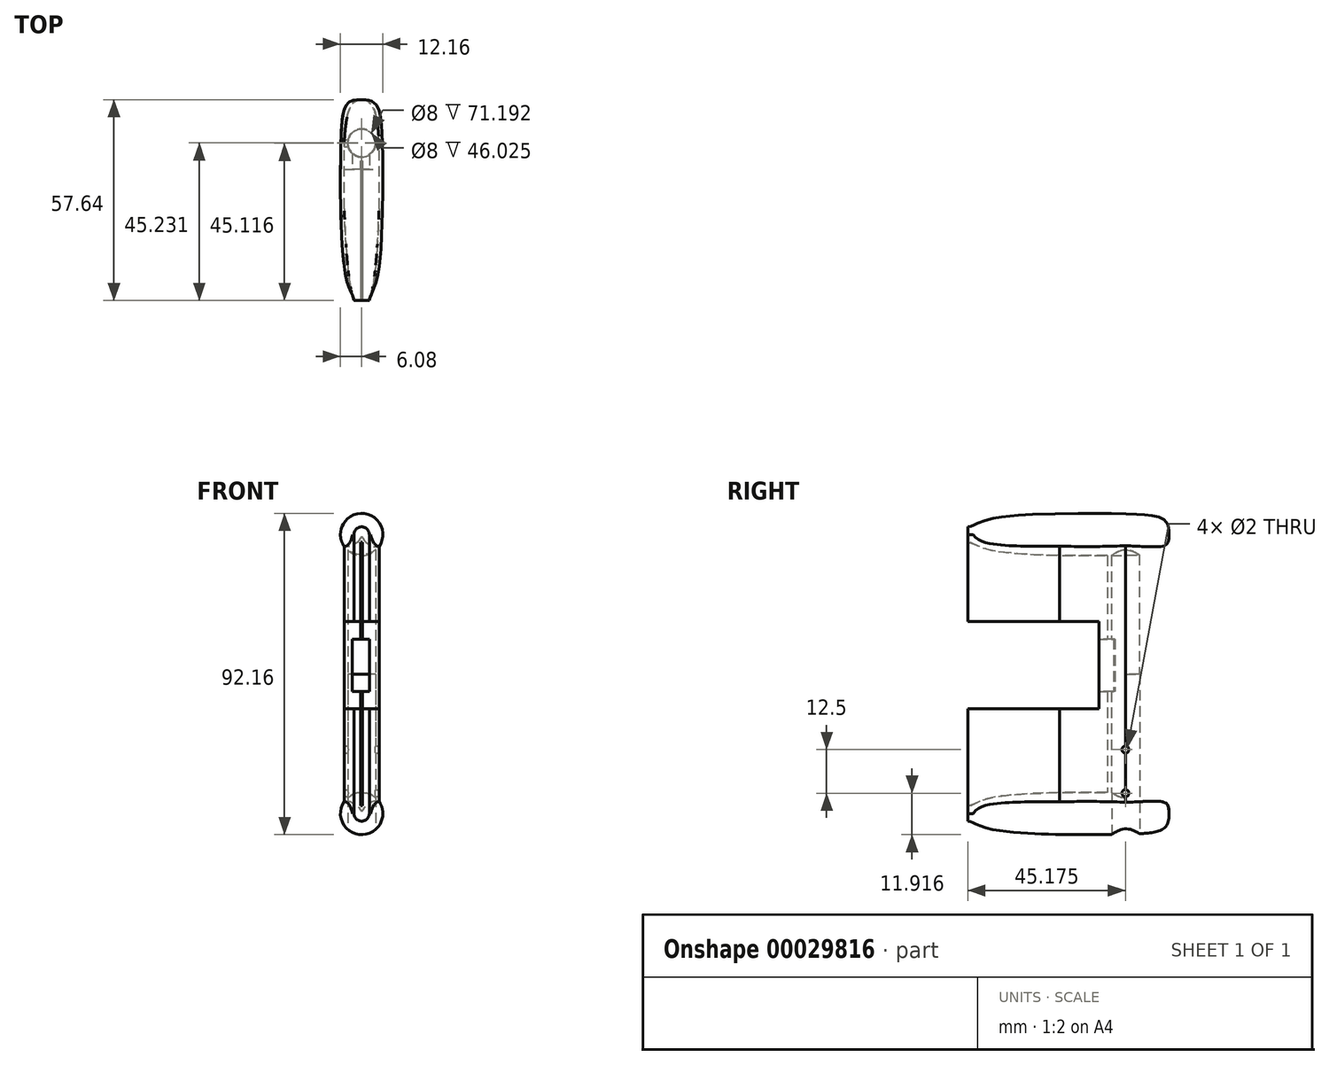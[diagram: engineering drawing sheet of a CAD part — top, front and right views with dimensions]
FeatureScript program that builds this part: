
annotation { "Feature Type Name" : "Feature", "Feature Type Description" : "" }
export const myFeature = defineFeature(function(context is Context, id is Id, definition is map)
    precondition{}
    {
        {
            var Q0;
            Q0=qCreatedBy(makeId("Top.planeOp"),FACE);
            var sketch = newSketch(context, id + "F0", { "sketchPlane" : qUnion([Q0])});
            skLineSegment(sketch, "E0", {"start": v(0, 90) * mm, "end": v(5, 90) * mm});
            skLineSegment(sketch, "E1", {"start": v(5, 90) * mm, "end": v(5, 10) * mm});
            skLineSegment(sketch, "E2", {"start": v(5, 10) * mm, "end": v(90, 10) * mm});
            skLineSegment(sketch, "E3", {"start": v(90, 10) * mm, "end": v(90, 0) * mm});
            skLineSegment(sketch, "E4", {"start": v(90, 0) * mm, "end": v(0, 0) * mm});
            skLineSegment(sketch, "E5.MirrorCS", {"start": v(0, 90) * mm, "end": v(-5, 90) * mm});
            skLineSegment(sketch, "E6.MirrorCS", {"start": v(-5, 90) * mm, "end": v(-5, 10) * mm});
            skLineSegment(sketch, "E7.MirrorCS", {"start": v(-5, 10) * mm, "end": v(-90, 10) * mm});
            skLineSegment(sketch, "E8.MirrorCS", {"start": v(-90, 10) * mm, "end": v(-90, 0) * mm});
            skLineSegment(sketch, "E9.MirrorCS", {"start": v(-90, 0) * mm, "end": v(0, 0) * mm});
            skSolve(sketch);
        }
        {
            var Q0;
            Q0=makeQuery(id+"F0.imprint","IMPRINT",FACE,{"disambiguationData":[TD([[makeQuery(id+"F0.imprint","IMPRINT",EDGE,{"derivedFrom":sQuery(id+"F0.wireOp",EDGE,"E0")}),-1.0]])]});
            extrude(context, id + "F1", {"entities" : qUnion([Q0]), "depth" : 10 * mm});
        }
        {
            var Q0;
            Q0=makeQuery(id+"F1.opExtrude","CAP_FACE",FACE,{"disambiguationData":[OSD([sQuery(id+"F0.wireOp",EDGE,"E0"),sQuery(id+"F0.wireOp",EDGE,"E1"),sQuery(id+"F0.wireOp",EDGE,"E2"),sQuery(id+"F0.wireOp",EDGE,"E3"),sQuery(id+"F0.wireOp",EDGE,"E4"),sQuery(id+"F0.wireOp",EDGE,"E5.MirrorCS"),sQuery(id+"F0.wireOp",EDGE,"E6.MirrorCS"),sQuery(id+"F0.wireOp",EDGE,"E7.MirrorCS"),sQuery(id+"F0.wireOp",EDGE,"E8.MirrorCS"),sQuery(id+"F0.wireOp",EDGE,"E9.MirrorCS")])],"isStart":false});
            var sketch = newSketch(context, id + "F2", { "sketchPlane" : qUnion([Q0])});
            skLineSegment(sketch, "E10.bottom", {"start": v(-5, 80) * mm, "end": v(5, 80) * mm});
            skLineSegment(sketch, "E10.top", {"start": v(-5, 70) * mm, "end": v(5, 70) * mm});
            skLineSegment(sketch, "E10.left", {"start": v(-5, 80) * mm, "end": v(-5, 70) * mm});
            skLineSegment(sketch, "E10.right", {"start": v(5, 80) * mm, "end": v(5, 70) * mm});
            skSolve(sketch);
        }
        {
            var Q0;
            Q0=makeQuery(id+"F2.imprint","IMPRINT",FACE,{"disambiguationData":[TD([[makeQuery(id+"F2.imprint","IMPRINT",EDGE,{"derivedFrom":sQuery(id+"F2.wireOp",EDGE,"E10.bottom")}),-1.0]])]});
            extrude(context, id + "F3", {"entities" : qUnion([Q0]), "operationType" : NewBodyOperationType.ADD, "depth" : 10 * mm});
        }
        {
            var Q0;
            {var subQ0=sQuery(id+"F0.wireOp",EDGE,"E1");var subQ1=sQuery(id+"F0.wireOp",EDGE,"E2");var subQ2=sQuery(id+"F0.wireOp",EDGE,"E3");var subQ3=sQuery(id+"F0.wireOp",EDGE,"E4");var subQ4=sQuery(id+"F0.wireOp",EDGE,"E6.MirrorCS");var subQ5=sQuery(id+"F0.wireOp",EDGE,"E7.MirrorCS");var subQ6=sQuery(id+"F0.wireOp",EDGE,"E8.MirrorCS");var subQ7=sQuery(id+"F0.wireOp",EDGE,"E9.MirrorCS");Q0=makeQuery(id+"F3.boolean.opBoolean","SPLIT",FACE,{"disambiguationData":[TD([makeQuery(id+"F1.opExtrude","SWEPT_FACE",FACE,{"disambiguationData":[OSD([subQ1])]})])],"derivedFrom":makeQuery(id+"F1.opExtrude","CAP_FACE",FACE,{"disambiguationData":[OSD([sQuery(id+"F0.wireOp",EDGE,"E0"),subQ0,subQ1,subQ2,subQ3,sQuery(id+"F0.wireOp",EDGE,"E5.MirrorCS"),subQ4,subQ5,subQ6,subQ7])],"isStart":false})});}
            var sketch = newSketch(context, id + "F4", { "sketchPlane" : qUnion([Q0])});
            skFitSpline(sketch, "E11", {"points": [v(0, 57.64) * mm, v(2.4, 56.63) * mm, v(5, 45.2) * mm, v(3.55, 6.02) * mm, v(2.2, 0) * mm], "startDerivative": vector(17.44, -0.09) * mm, "endDerivative": vector(-5.28, -21) * mm});
            skLineSegment(sketch, "E12", {"start": v(0, 57.64) * mm, "end": v(0, 24.79) * mm, "construction": true});
            skLineSegment(sketch, "E13", {"start": v(2.2, 0) * mm, "end": v(0.25, 0) * mm});
            skLineSegment(sketch, "E14", {"start": v(0.25, 0) * mm, "end": v(0.25, 40) * mm});
            skLineSegment(sketch, "E15", {"start": v(0.25, 40) * mm, "end": v(0, 40) * mm});
            skFitSpline(sketch, "E16.MirrorCS", {"points": [v(0, 57.64) * mm, v(-2.4, 56.63) * mm, v(-5, 45.2) * mm, v(-3.55, 6.02) * mm, v(-2.2, 0) * mm], "startDerivative": vector(-17.44, -0.09) * mm, "endDerivative": vector(5.28, -21) * mm});
            skLineSegment(sketch, "E17.MirrorCS", {"start": v(-0.25, 40) * mm, "end": v(0, 40) * mm});
            skLineSegment(sketch, "E18.MirrorCS", {"start": v(-0.25, 0) * mm, "end": v(-0.25, 40) * mm});
            skLineSegment(sketch, "E19.MirrorCS", {"start": v(-2.2, 0) * mm, "end": v(-0.25, 0) * mm});
            skPoint(sketch, "E20.rect.middle", {"position": v(0, 45.12) * mm});
            skCircle(sketch, "E21", {"center": v(0, 45.12) * mm, "radius": 4 * mm});
            skSolve(sketch);
        }
        {
            var Q0;
            {var subQ19=sQuery(id+"F4.wireOp",EDGE,"E13");Q0=makeQuery(id+"F4.imprint","IMPRINT",FACE,{"disambiguationData":[TD([[makeQuery(id+"F4.imprint","IMPRINT",EDGE,{"derivedFrom":subQ19}),1.0]])]});}
            extrude(context, id + "F5", {"entities" : qUnion([Q0]), "operationType" : NewBodyOperationType.ADD, "depth" : 130 * mm});
        }
        {
            var Q0;
            Q0=qCreatedBy(makeId("Right.planeOp"),FACE);
            var sketch = newSketch(context, id + "F6", { "sketchPlane" : qUnion([Q0])});
            skLineSegment(sketch, "E22.bottom", {"start": v(-13.73, 90) * mm, "end": v(37.64, 90) * mm});
            skLineSegment(sketch, "E22.top", {"start": v(-13.73, 115) * mm, "end": v(37.64, 115) * mm});
            skLineSegment(sketch, "E22.left", {"start": v(-13.73, 90) * mm, "end": v(-13.73, 115) * mm});
            skLineSegment(sketch, "E22.right", {"start": v(37.64, 90) * mm, "end": v(37.64, 115) * mm});
            skSolve(sketch);
        }
        {
            var Q0;
            Q0=makeQuery(id+"F6.imprint","IMPRINT",FACE,{"disambiguationData":[TD([[makeQuery(id+"F6.imprint","IMPRINT",EDGE,{"derivedFrom":sQuery(id+"F6.wireOp",EDGE,"E22.bottom")}),1.0]])]});
            extrude(context, id + "F7", {"entities" : qUnion([Q0]), "operationType" : NewBodyOperationType.REMOVE, "endBound" : BoundingType.THROUGH_ALL, "oppositeDirection" : true, "depth" : 25 * mm, "hasSecondDirection" : true, "secondDirectionBound" : SecondDirectionBoundingType.THROUGH_ALL, "secondDirectionOppositeDirection" : false, "secondDirectionDepth" : 25 * mm});
        }
        {
            var Q0;
            Q0=qCreatedBy(makeId("Top.planeOp"),FACE);
            var sketch = newSketch(context, id + "F8", { "sketchPlane" : qUnion([Q0])});
            skLineSegment(sketch, "E23.rect.bottom", {"start": v(115.77, -104.9) * mm, "end": v(-115.77, -104.9) * mm});
            skLineSegment(sketch, "E23.rect.top", {"start": v(115.77, 104.9) * mm, "end": v(-115.77, 104.9) * mm});
            skLineSegment(sketch, "E23.rect.left", {"start": v(115.77, -104.9) * mm, "end": v(115.77, 104.9) * mm});
            skLineSegment(sketch, "E23.rect.right", {"start": v(-115.77, -104.9) * mm, "end": v(-115.77, 104.9) * mm});
            skPoint(sketch, "E23.rect.middle", {"position": v(0, 0) * mm});
            skSolve(sketch);
        }
        {
            var Q0;
            Q0=qSketchRegion(id+"F8",true);
            var Q1;
            Q1=makeQuery(id+"F3.opExtrude","CAP_FACE",FACE,{"disambiguationData":[OSD([sQuery(id+"F2.wireOp",EDGE,"E10.bottom"),sQuery(id+"F2.wireOp",EDGE,"E10.top"),sQuery(id+"F2.wireOp",EDGE,"E10.left"),sQuery(id+"F2.wireOp",EDGE,"E10.right")])],"isStart":false});
            extrude(context, id + "F9", {"entities" : qUnion([Q0]), "operationType" : NewBodyOperationType.REMOVE, "endBound" : BoundingType.UP_TO_SURFACE, "endBoundEntityFace" : qUnion([Q1]), "depth" : 25 * mm});
        }
        {
            var Q0;
            Q0=qCreatedBy(makeId("Right.planeOp"),FACE);
            var sketch = newSketch(context, id + "F10", { "sketchPlane" : qUnion([Q0])});
            skCircle(sketch, "E24", {"center": v(45.18, 28.34) * mm, "radius": 1 * mm});
            skCircle(sketch, "E25.1.0.0", {"center": v(45.18, 40.84) * mm, "radius": 1 * mm});
            skCircle(sketch, "E25.2.0.0", {"center": v(45.18, 53.34) * mm, "radius": 1 * mm});
            skLineSegment(sketch, "E25.direction1", {"start": v(45.18, 28.34) * mm, "end": v(45.18, 40.84) * mm, "construction": true});
            skCircle(sketch, "E26.0.3.0", {"center": v(45.18, 65.84) * mm, "radius": 1 * mm});
            skCircle(sketch, "E26.0.4.0", {"center": v(45.18, 78.34) * mm, "radius": 1 * mm});
            skSolve(sketch);
        }
        {
            var Q0;
            Q0=qSketchRegion(id+"F10",true);
            extrude(context, id + "F11", {"entities" : qUnion([Q0]), "operationType" : NewBodyOperationType.REMOVE, "endBound" : BoundingType.THROUGH_ALL, "oppositeDirection" : true, "depth" : 25 * mm, "hasSecondDirection" : true, "secondDirectionBound" : SecondDirectionBoundingType.THROUGH_ALL, "secondDirectionOppositeDirection" : false, "secondDirectionDepth" : 25 * mm});
        }
        {
            var Q0;
            Q0=qCreatedBy(makeId("Right.planeOp"),FACE);
            var sketch = newSketch(context, id + "F12", { "sketchPlane" : qUnion([Q0])});
            skLineSegment(sketch, "E27.bottom", {"start": v(78.93, -35.32) * mm, "end": v(-26.83, -35.32) * mm});
            skLineSegment(sketch, "E27.top", {"start": v(78.93, 60) * mm, "end": v(-26.83, 60) * mm});
            skLineSegment(sketch, "E27.left", {"start": v(78.93, -35.32) * mm, "end": v(78.93, 60) * mm});
            skLineSegment(sketch, "E27.right", {"start": v(-26.83, -35.32) * mm, "end": v(-26.83, 60) * mm});
            skSolve(sketch);
        }
        {
            var Q0;
            Q0=makeQuery(id+"F12.imprint","IMPRINT",FACE,{"disambiguationData":[TD([[makeQuery(id+"F12.imprint","IMPRINT",EDGE,{"derivedFrom":sQuery(id+"F12.wireOp",EDGE,"E27.bottom")}),-1.0]])]});
            extrude(context, id + "F13", {"entities" : qUnion([Q0]), "operationType" : NewBodyOperationType.REMOVE, "endBound" : BoundingType.SYMMETRIC, "oppositeDirection" : true, "depth" : 30 * mm});
        }
        {
            var Q0;
            Q0=makeQuery(id+"F5.opExtrude","CAP_FACE",FACE,{"disambiguationData":[OSD([sQuery(id+"F4.wireOp",EDGE,"E11"),sQuery(id+"F4.wireOp",EDGE,"E13"),sQuery(id+"F4.wireOp",EDGE,"E14"),sQuery(id+"F4.wireOp",EDGE,"E15"),sQuery(id+"F4.wireOp",EDGE,"E16.MirrorCS"),sQuery(id+"F4.wireOp",EDGE,"E17.MirrorCS"),sQuery(id+"F4.wireOp",EDGE,"E18.MirrorCS"),sQuery(id+"F4.wireOp",EDGE,"E19.MirrorCS"),sQuery(id+"F4.wireOp",EDGE,"E20.rect.bottom"),sQuery(id+"F4.wireOp",EDGE,"E20.rect.top"),sQuery(id+"F4.wireOp",EDGE,"E20.rect.left"),sQuery(id+"F4.wireOp",EDGE,"E20.rect.right")])],"isStart":false});
            var sketch = newSketch(context, id + "F14", { "sketchPlane" : qUnion([Q0])});
            skFitSpline(sketch, "E28.0", {"points": [v(0, 57.64) * mm, v(-0.68, 57.64) * mm, v(-3.7, 56.8) * mm, v(-5.96, 44.64) * mm, v(-4.46, 6.49) * mm, v(-2.52, 1.26) * mm, v(-2.2, 0) * mm]});
            skLineSegment(sketch, "E29", {"start": v(-0.25, 0) * mm, "end": v(0, 0) * mm});
            skLineSegment(sketch, "E30", {"start": v(0, 0) * mm, "end": v(0, 57.64) * mm});
            skLineSegment(sketch, "E31.0", {"start": v(-5, 45.2) * mm, "end": v(-5, 26.34) * mm});
            skFitSpline(sketch, "E32.0", {"points": [v(0, 57.64) * mm, v(-0.68, 57.64) * mm, v(-3.7, 56.8) * mm, v(-5.96, 44.64) * mm, v(-4.46, 6.49) * mm, v(-2.52, 1.26) * mm, v(-2.2, 0) * mm]});
            skFitSpline(sketch, "E33.0", {"points": [v(0, 57.64) * mm, v(-0.68, 57.64) * mm, v(-3.7, 56.8) * mm, v(-5.96, 44.64) * mm, v(-4.46, 6.49) * mm, v(-2.52, 1.26) * mm, v(-2.2, 0) * mm]});
            skLineSegment(sketch, "E33.1", {"start": v(-2.2, 0) * mm, "end": v(-0.25, 0) * mm});
            skSolve(sketch);
        }
        {
            var Q0;
            Q0=qSketchRegion(id+"F14",true);
            var Q1;
            Q1=sQuery(id+"F14.wireOp",EDGE,"E30");
            revolve(context, id + "F15", {"operationType" : NewBodyOperationType.ADD, "entities" : qUnion([Q0]), "axis" : qUnion([Q1]), "revolveType" : RevolveType.FULL});
        }
        {
            var Q0;
            {var subQ0=sQuery(id+"F0.wireOp",EDGE,"E6.MirrorCS");Q0=makeQuery(id+"F7.boolean.opBoolean","COPY",FACE,{"disambiguationData":[TD([makeQuery(id+"F1.opExtrude","SWEPT_FACE",FACE,{"disambiguationData":[OSD([subQ0])]})])],"derivedFrom":makeQuery(id+"F7.opExtrude","SWEPT_FACE",FACE,{"disambiguationData":[OSD([sQuery(id+"F6.wireOp",EDGE,"E22.right")])]})});}
            var sketch = newSketch(context, id + "F16", { "sketchPlane" : qUnion([Q0])});
            skLineSegment(sketch, "E34.rect.bottom", {"start": v(2.25, 95) * mm, "end": v(-2.75, 95) * mm});
            skLineSegment(sketch, "E34.rect.top", {"start": v(2.25, 110) * mm, "end": v(-2.75, 110) * mm});
            skLineSegment(sketch, "E34.rect.left", {"start": v(2.25, 95) * mm, "end": v(2.25, 110) * mm});
            skLineSegment(sketch, "E34.rect.right", {"start": v(-2.75, 95) * mm, "end": v(-2.75, 110) * mm});
            skPoint(sketch, "E34.rect.middle", {"position": v(-0.25, 102.5) * mm});
            skSolve(sketch);
        }
        {
            var Q0;
            Q0 = qSketchRegion(id + "F16", true);
            extrude(context, id + "F17", {"entities" : qUnion([Q0]), "operationType" : NewBodyOperationType.REMOVE, "oppositeDirection" : true, "depth" : 10 * mm});
        }
        {
            var Q0;
            Q0=makeQuery(id+"F13.boolean.opBoolean","COPY",FACE,{"derivedFrom":makeQuery(id+"F13.opExtrude","SWEPT_FACE",FACE,{"disambiguationData":[OSD([sQuery(id+"F12.wireOp",EDGE,"E27.top")])]})});
            var sketch = newSketch(context, id + "F18", { "sketchPlane" : qUnion([Q0])});
            skLineSegment(sketch, "E35", {"start": v(0, 0) * mm, "end": v(0, -57.64) * mm});
            skFitSpline(sketch, "E36.0", {"points": [v(0, -57.64) * mm, v(0.68, -57.64) * mm, v(3.7, -56.8) * mm, v(5.96, -44.64) * mm, v(4.46, -6.49) * mm, v(2.52, -1.26) * mm, v(2.2, 0) * mm]});
            skLineSegment(sketch, "E36.1", {"start": v(5, -45.2) * mm, "end": v(5, -26.34) * mm});
            skFitSpline(sketch, "E36.2", {"points": [v(0, -57.64) * mm, v(0.68, -57.64) * mm, v(3.7, -56.8) * mm, v(5.96, -44.64) * mm, v(4.46, -6.49) * mm, v(2.52, -1.26) * mm, v(2.2, 0) * mm]});
            skLineSegment(sketch, "E36.3", {"start": v(0.25, 0) * mm, "end": v(2.2, 0) * mm});
            skLineSegment(sketch, "E37", {"start": v(0.25, 0) * mm, "end": v(0, 0) * mm});
            skSolve(sketch);
        }
        {
            var Q0;
            Q0 = qSketchRegion(id + "F18", true);
            var Q1;
            Q1=sQuery(id+"F18.wireOp",EDGE,"E35");
            revolve(context, id + "F19", {"operationType" : NewBodyOperationType.ADD, "entities" : qUnion([Q0]), "axis" : qUnion([Q1]), "revolveType" : RevolveType.FULL});
        }
        {
            var Q0;
            Q0=qCreatedBy(makeId("Top.planeOp"),FACE);
            var sketch = newSketch(context, id + "F20", { "sketchPlane" : qUnion([Q0])});
            skCircle(sketch, "E38", {"center": v(0, 45.23) * mm, "radius": 4 * mm});
            skSolve(sketch);
        }
        {
            var Q0;
            Q0 = qSketchRegion(id + "F20", true);
            extrude(context, id + "F21", {"entities" : qUnion([Q0]), "operationType" : NewBodyOperationType.REMOVE, "depth" : 100 * mm});
        }
    });
